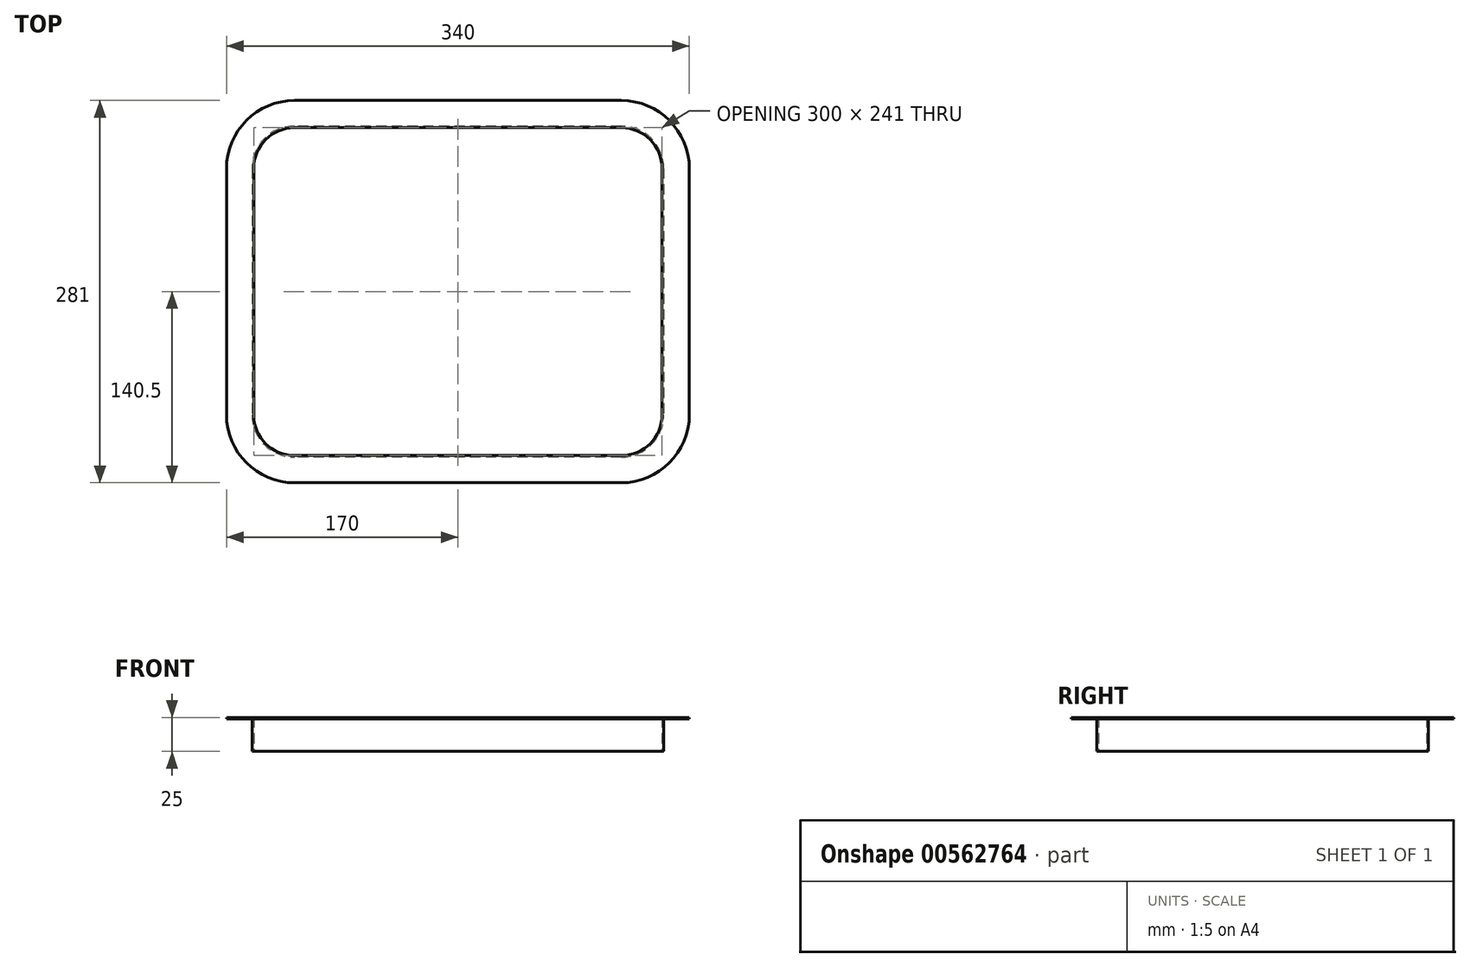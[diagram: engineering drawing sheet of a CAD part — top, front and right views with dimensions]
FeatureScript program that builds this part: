
annotation { "Feature Type Name" : "Feature", "Feature Type Description" : "" }
export const myFeature = defineFeature(function(context is Context, id is Id, definition is map)
    precondition{}
    {
        {
            var Q0;
            Q0=qCreatedBy(makeId("Top.planeOp"),FACE);
            var sketch = newSketch(context, id + "F0", { "sketchPlane" : qUnion([Q0])});
            skLineSegment(sketch, "E0.bottom", {"start": v(120, 140.5) * mm, "end": v(-120, 140.5) * mm});
            skLineSegment(sketch, "E0.top", {"start": v(120, -140.5) * mm, "end": v(-120, -140.5) * mm});
            skLineSegment(sketch, "E0.left", {"start": v(170, 90.5) * mm, "end": v(170, -90.5) * mm});
            skLineSegment(sketch, "E0.right", {"start": v(-170, 90.5) * mm, "end": v(-170, -90.5) * mm});
            skPoint(sketch, "E0.middle", {"position": v(0, 0) * mm});
            skLineSegment(sketch, "E1.0", {"start": v(150, 90.5) * mm, "end": v(150, -90.5) * mm});
            skLineSegment(sketch, "E1.1", {"start": v(120, 120.5) * mm, "end": v(-120, 120.5) * mm});
            skLineSegment(sketch, "E1.2", {"start": v(-150, 90.5) * mm, "end": v(-150, -90.5) * mm});
            skLineSegment(sketch, "E1.3", {"start": v(120, -120.5) * mm, "end": v(-120, -120.5) * mm});
            skPoint(sketch, "E2.visualSharp", {"position": v(170, 140.5) * mm});
            skArc(sketch, "E2.filletArc", {"start": v(170, 90.5) * mm, "mid": v(155.36, 125.86) * mm, "end": v(120, 140.5) * mm});
            skPoint(sketch, "E3.visualSharp", {"position": v(170, -140.5) * mm});
            skArc(sketch, "E3.filletArc", {"start": v(120, -140.5) * mm, "mid": v(155.36, -125.86) * mm, "end": v(170, -90.5) * mm});
            skPoint(sketch, "E4.visualSharp", {"position": v(-170, -140.5) * mm});
            skArc(sketch, "E4.filletArc", {"start": v(-170, -90.5) * mm, "mid": v(-155.36, -125.86) * mm, "end": v(-120, -140.5) * mm});
            skPoint(sketch, "E5.visualSharp", {"position": v(-170, 140.5) * mm});
            skArc(sketch, "E5.filletArc", {"start": v(-120, 140.5) * mm, "mid": v(-155.36, 125.86) * mm, "end": v(-170, 90.5) * mm});
            skPoint(sketch, "E6.visualSharp", {"position": v(150, -120.5) * mm});
            skArc(sketch, "E6.filletArc", {"start": v(120, -120.5) * mm, "mid": v(141.21, -111.71) * mm, "end": v(150, -90.5) * mm});
            skPoint(sketch, "E7.visualSharp", {"position": v(150, 120.5) * mm});
            skArc(sketch, "E7.filletArc", {"start": v(150, 90.5) * mm, "mid": v(141.21, 111.71) * mm, "end": v(120, 120.5) * mm});
            skPoint(sketch, "E8.visualSharp", {"position": v(-150, 120.5) * mm});
            skArc(sketch, "E8.filletArc", {"start": v(-120, 120.5) * mm, "mid": v(-141.21, 111.71) * mm, "end": v(-150, 90.5) * mm});
            skPoint(sketch, "E9.visualSharp", {"position": v(-150, -120.5) * mm});
            skArc(sketch, "E9.filletArc", {"start": v(-150, -90.5) * mm, "mid": v(-141.21, -111.71) * mm, "end": v(-120, -120.5) * mm});
            skSolve(sketch);
        }
        {
            var Q0;
            Q0 = qSketchRegion(id + "F0", true);
            extrude(context, id + "F1", {"entities" : qUnion([Q0]), "depth" : 1.2 * mm, "offsetDistance" : 25 * mm});
        }
        {
            var Q0;
            Q0=makeQuery(id+"F1.opExtrude","CAP_FACE",FACE,{"disambiguationData":[OSD([sQuery(id+"F0.wireOp",EDGE,"E0.bottom"),sQuery(id+"F0.wireOp",EDGE,"E0.top"),sQuery(id+"F0.wireOp",EDGE,"E0.left"),sQuery(id+"F0.wireOp",EDGE,"E0.right"),sQuery(id+"F0.wireOp",EDGE,"E1.0"),sQuery(id+"F0.wireOp",EDGE,"E1.1"),sQuery(id+"F0.wireOp",EDGE,"E1.2"),sQuery(id+"F0.wireOp",EDGE,"E1.3"),sQuery(id+"F0.wireOp",EDGE,"E2.filletArc"),sQuery(id+"F0.wireOp",EDGE,"E3.filletArc"),sQuery(id+"F0.wireOp",EDGE,"E4.filletArc"),sQuery(id+"F0.wireOp",EDGE,"E5.filletArc"),sQuery(id+"F0.wireOp",EDGE,"E6.filletArc"),sQuery(id+"F0.wireOp",EDGE,"E7.filletArc"),sQuery(id+"F0.wireOp",EDGE,"E8.filletArc"),sQuery(id+"F0.wireOp",EDGE,"E9.filletArc")])],"isStart":true});
            var sketch = newSketch(context, id + "F2", { "sketchPlane" : qUnion([Q0])});
            skLineSegment(sketch, "E10.0", {"start": v(120, -120.5) * mm, "end": v(-120, -120.5) * mm});
            skArc(sketch, "E11.0", {"start": v(150, -90.5) * mm, "mid": v(141.21, -111.71) * mm, "end": v(120, -120.5) * mm});
            skLineSegment(sketch, "E12.0", {"start": v(150, -90.5) * mm, "end": v(150, 90.5) * mm});
            skArc(sketch, "E13.0", {"start": v(120, 120.5) * mm, "mid": v(141.21, 111.71) * mm, "end": v(150, 90.5) * mm});
            skLineSegment(sketch, "E14.0", {"start": v(120, 120.5) * mm, "end": v(-120, 120.5) * mm});
            skArc(sketch, "E15.0", {"start": v(-150, 90.5) * mm, "mid": v(-141.21, 111.71) * mm, "end": v(-120, 120.5) * mm});
            skLineSegment(sketch, "E16.0", {"start": v(-150, -90.5) * mm, "end": v(-150, 90.5) * mm});
            skArc(sketch, "E17.0", {"start": v(-120, -120.5) * mm, "mid": v(-141.21, -111.71) * mm, "end": v(-150, -90.5) * mm});
            skArc(sketch, "E18.0", {"start": v(151.2, -90.5) * mm, "mid": v(142.06, -112.56) * mm, "end": v(120, -121.7) * mm});
            skLineSegment(sketch, "E18.1", {"start": v(151.2, -90.5) * mm, "end": v(151.2, 90.5) * mm});
            skLineSegment(sketch, "E18.2", {"start": v(120, -121.7) * mm, "end": v(-120, -121.7) * mm});
            skArc(sketch, "E18.3", {"start": v(120, 121.7) * mm, "mid": v(142.06, 112.56) * mm, "end": v(151.2, 90.5) * mm});
            skArc(sketch, "E18.4", {"start": v(-120, -121.7) * mm, "mid": v(-142.06, -112.56) * mm, "end": v(-151.2, -90.5) * mm});
            skLineSegment(sketch, "E18.5", {"start": v(-151.2, -90.5) * mm, "end": v(-151.2, 90.5) * mm});
            skArc(sketch, "E18.6", {"start": v(-151.2, 90.5) * mm, "mid": v(-142.06, 112.56) * mm, "end": v(-120, 121.7) * mm});
            skLineSegment(sketch, "E18.7", {"start": v(120, 121.7) * mm, "end": v(-120, 121.7) * mm});
            skSolve(sketch);
        }
        {
            var Q0;
            Q0 = qSketchRegion(id + "F2", true);
            extrude(context, id + "F3", {"entities" : qUnion([Q0]), "operationType" : NewBodyOperationType.ADD, "depth" : 23.8 * mm, "offsetDistance" : 25 * mm});
        }
    });
